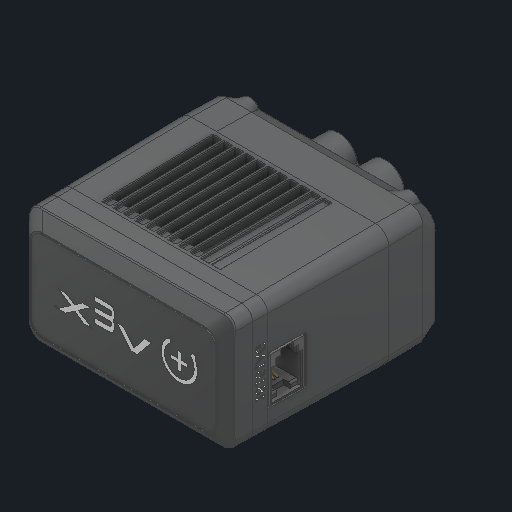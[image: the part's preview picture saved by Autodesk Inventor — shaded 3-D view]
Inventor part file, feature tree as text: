
AUTODESK INVENTOR PART (.ipt)
format: ipt  version: 2025 (Build 290162000, 162)  size: 13,153,280 bytes
history: native  units: in
note: dims shown in document units (in); Inventor stores cm internally (conversion verified against a paired STEP export)
features: other x19, sketch x2
ambient origin geometry x8: Origin, YZ Plane, XZ Plane, XY Plane, X Axis, Y Axis, Z Axis, Center Point
bodies: Solid1 (feature_tree), Solid2 (feature_tree), Solid7 (feature_tree), Solid8 (feature_tree), Solid9 (feature_tree), Solid20 (feature_tree), Solid21 (feature_tree), Solid22 (feature_tree)
feature tree (21):
  other  "V5 Motor.ipt"
  other  "Solid1::V5 Motor.ipt"
  other  "Solid2::V5 Motor.ipt"
  other  "Solid4::V5 Motor.ipt"
  other  "Solid6::V5 Motor.ipt"
  other  "Solid7::V5 Motor.ipt"
  other  "Solid8::V5 Motor.ipt"
  other  "Solid9::V5 Motor.ipt"
  other  "Solid14::V5 Motor.ipt"
  other  "Solid16::V5 Motor.ipt"
  other  "Solid17::V5 Motor.ipt"
  other  "Solid18::V5 Motor.ipt"
  other  "Solid19::V5 Motor.ipt"
  other  "Solid20::V5 Motor.ipt"
  other  "Solid21::V5 Motor.ipt"
  other  "Solid22::V5 Motor.ipt"
  other  "TaggingFeature1"
  sketch  "Sketch1"  dims[d0=0.3937in]
  sketch  "Sketch2"  dims[d4=0.0in d5=0.0in]
  other  "iInsert:1"
  other  "iInsert:2"
